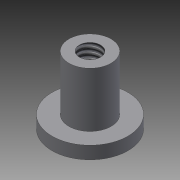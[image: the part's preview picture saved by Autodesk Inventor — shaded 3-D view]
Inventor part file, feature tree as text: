
AUTODESK INVENTOR PART (.ipt)
format: ipt  version: 2015 (Build 190159000, 159)  size: 88,576 bytes
history: native  units: in
note: dims shown in document units (in); Inventor stores cm internally (conversion verified against a paired STEP export)
features: revolve x1, hole x1, sketch x1
ambient origin geometry x8: Origin, YZ Plane, XZ Plane, XY Plane, X Axis, Y Axis, Z Axis, Center Point
bodies: Solid1 (feature_tree)
feature tree (3):
  revolve  "Revolution1"  [1 undecoded]
  hole  "Hole1"  [1 undecoded]
  sketch  "Sketch1"  dims[d0=1.0in d1=0.188in d2=0.3125in d3=0.5625in d4=90.0deg d14=1.0in d15=1.0in d7=0.315in d8=1.0in d9=0.375in d10=0.25in d11=0.5635in d12=1.259in d13=0.8108in]
note: 2 required parameter values undecoded (feature->parameter linkage not recoverable at this tier; creation-order binding heuristic only, values carry confidence <= 0.55)